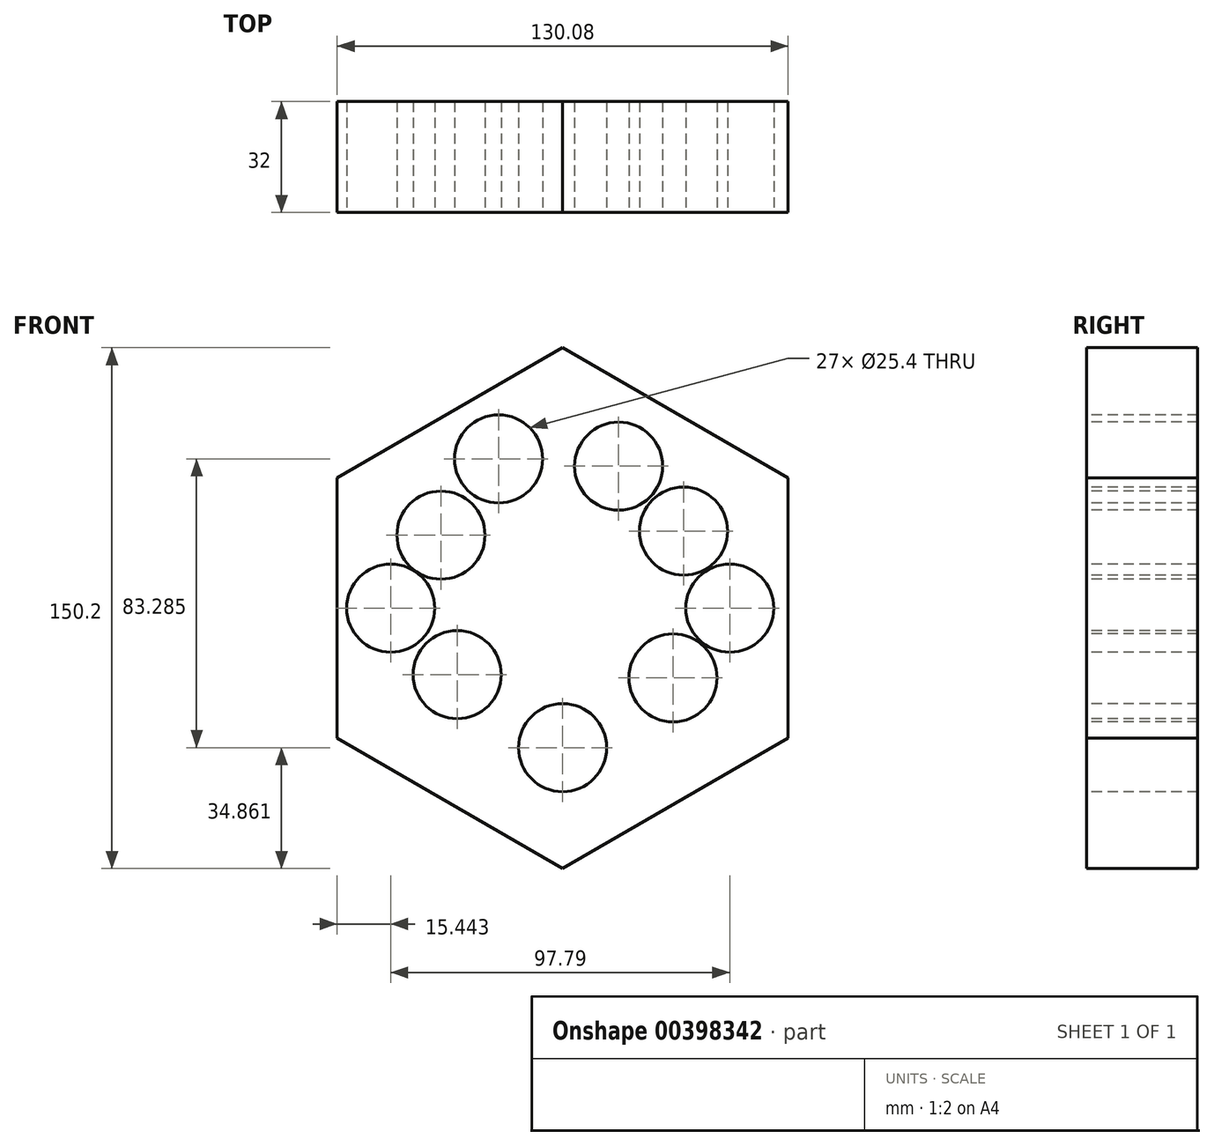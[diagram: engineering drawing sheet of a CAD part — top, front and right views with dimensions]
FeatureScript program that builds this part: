
annotation { "Feature Type Name" : "Feature", "Feature Type Description" : "" }
export const myFeature = defineFeature(function(context is Context, id is Id, definition is map)
    precondition{}
    {
        {
            var Q0;
            Q0=qCreatedBy(makeId("Front.planeOp"),FACE);
            var sketch = newSketch(context, id + "F0", { "sketchPlane" : qUnion([Q0])});
            skCircle(sketch, "E0.cCircle", {"center": v(0, 0) * mm, "radius": 65.04 * mm, "construction": true});
            skLineSegment(sketch, "E0.0", {"start": v(65.04, 37.55) * mm, "end": v(65.04, -37.55) * mm});
            skLineSegment(sketch, "E0.1", {"start": v(65.04, -37.55) * mm, "end": v(0, -75.1) * mm});
            skLineSegment(sketch, "E0.2", {"start": v(0, -75.1) * mm, "end": v(-65.04, -37.55) * mm});
            skLineSegment(sketch, "E0.3", {"start": v(-65.04, -37.55) * mm, "end": v(-65.04, 37.55) * mm});
            skLineSegment(sketch, "E0.4", {"start": v(-65.04, 37.55) * mm, "end": v(0, 75.1) * mm});
            skLineSegment(sketch, "E0.5", {"start": v(0, 75.1) * mm, "end": v(65.04, 37.55) * mm});
            skPoint(sketch, "E0.0.midPoint", {"position": v(65.04, 0) * mm});
            skSolve(sketch);
        }
        {
            var Q0;
            Q0=qCreatedBy(makeId("Front.planeOp"),FACE);
            var sketch = newSketch(context, id + "F1", { "sketchPlane" : qUnion([Q0])});
            skEllipse(sketch, "E1", {"center": v(-35.1, 21.06) * mm, "majorRadius": 29.5 * mm, "minorRadius": 7.58 * mm, "majorAxis": v(0.92, -0.38)});
            skSolve(sketch);
        }
        {
            var Q0;
            Q0=makeQuery(id+"F0.imprint","IMPRINT",FACE,{"disambiguationData":[TD([[makeQuery(id+"F0.imprint","IMPRINT",EDGE,{"derivedFrom":sQuery(id+"F0.wireOp",EDGE,"E0.0")}),-1.0]])]});
            var sketch = newSketch(context, id + "F2", { "sketchPlane" : qUnion([Q0])});
            skEllipse(sketch, "E2", {"center": v(34.86, 22.23) * mm, "majorRadius": 25.9 * mm, "minorRadius": 9.15 * mm, "majorAxis": v(-0.77, -0.64)});
            skSolve(sketch);
        }
        {
            var Q0;
            Q0=makeQuery(id+"F0.imprint","IMPRINT",FACE,{"disambiguationData":[TD([[makeQuery(id+"F0.imprint","IMPRINT",EDGE,{"derivedFrom":sQuery(id+"F0.wireOp",EDGE,"E0.0")}),-1.0]])]});
            var sketch = newSketch(context, id + "F3", { "sketchPlane" : qUnion([Q0])});
            skEllipse(sketch, "E3", {"center": v(-30.41, -19.18) * mm, "majorRadius": 31.91 * mm, "minorRadius": 8.43 * mm, "majorAxis": v(-0.9, -0.45)});
            skSolve(sketch);
        }
        {
            var Q0;
            Q0=makeQuery(id+"F0.imprint","IMPRINT",FACE,{"disambiguationData":[TD([[makeQuery(id+"F0.imprint","IMPRINT",EDGE,{"derivedFrom":sQuery(id+"F0.wireOp",EDGE,"E0.0")}),-1.0]])]});
            var sketch = newSketch(context, id + "F4", { "sketchPlane" : qUnion([Q0])});
            skEllipse(sketch, "E4", {"center": v(31.82, -20.12) * mm, "majorRadius": 33.8 * mm, "minorRadius": 8.23 * mm, "majorAxis": v(0.9, -0.44)});
            skSolve(sketch);
        }
        {
            var Q0;
            Q0=makeQuery(id+"F0.imprint","IMPRINT",FACE,{"disambiguationData":[TD([[makeQuery(id+"F0.imprint","IMPRINT",EDGE,{"derivedFrom":sQuery(id+"F0.wireOp",EDGE,"E0.0")}),-1.0]])]});
            var sketch = newSketch(context, id + "F5", { "sketchPlane" : qUnion([Q0])});
            skCircle(sketch, "E5", {"center": v(-18.48, 43.05) * mm, "radius": 13.64 * mm});
            skSolve(sketch);
        }
        {
            var Q0;
            Q0=makeQuery(id+"F0.imprint","IMPRINT",FACE,{"disambiguationData":[TD([[makeQuery(id+"F0.imprint","IMPRINT",EDGE,{"derivedFrom":sQuery(id+"F0.wireOp",EDGE,"E0.0")}),-1.0]])]});
            var sketch = newSketch(context, id + "F6", { "sketchPlane" : qUnion([Q0])});
            skCircle(sketch, "E6", {"center": v(-49.6, 0) * mm, "radius": 11.14 * mm});
            skSolve(sketch);
        }
        {
            var Q0;
            Q0=makeQuery(id+"F0.imprint","IMPRINT",FACE,{"disambiguationData":[TD([[makeQuery(id+"F0.imprint","IMPRINT",EDGE,{"derivedFrom":sQuery(id+"F0.wireOp",EDGE,"E0.0")}),-1.0]])]});
            var sketch = newSketch(context, id + "F7", { "sketchPlane" : qUnion([Q0])});
            skCircle(sketch, "E7", {"center": v(16.14, 40.94) * mm, "radius": 12.82 * mm});
            skCircle(sketch, "E8", {"center": v(48.2, 0) * mm, "radius": 13.44 * mm});
            skCircle(sketch, "E9", {"center": v(0, -40.24) * mm, "radius": 16.75 * mm});
            skSolve(sketch);
        }
        {
            var Q0;
            Q0=makeQuery(id+"F0.imprint","IMPRINT",FACE,{"disambiguationData":[TD([[makeQuery(id+"F0.imprint","IMPRINT",EDGE,{"derivedFrom":sQuery(id+"F0.wireOp",EDGE,"E0.0")}),-1.0]])]});
            extrude(context, id + "F8", {"entities" : qUnion([Q0]), "oppositeDirection" : true, "depth" : 32 * mm});
        }
        {
            var Q0;
            Q0=sQuery(id+"F5.wireOp",VERTEX,"E5.center");
            var Q1;
            Q1=sQuery(id+"F7.wireOp",VERTEX,"E7.center");
            var Q2;
            Q2=sQuery(id+"F2.wireOp",VERTEX,"E2.center");
            var Q3;
            Q3=sQuery(id+"F7.wireOp",VERTEX,"E8.center");
            var Q4;
            Q4=sQuery(id+"F7.wireOp",VERTEX,"E9.center");
            var Q5;
            Q5=sQuery(id+"F3.wireOp",VERTEX,"E3.center");
            var Q6;
            Q6=sQuery(id+"F6.wireOp",VERTEX,"E6.center");
            var Q7;
            Q7=sQuery(id+"F1.wireOp",VERTEX,"E1.center");
            var Q8;
            Q8=sQuery(id+"F4.wireOp",VERTEX,"E4.center");
            var Q9;
            Q9=makeQuery(id+"F8.opExtrude","SWEPT_BODY",BODY,{"disambiguationData":[OSD([sQuery(id+"F0.wireOp",EDGE,"E0.0"),sQuery(id+"F0.wireOp",EDGE,"E0.1"),sQuery(id+"F0.wireOp",EDGE,"E0.2"),sQuery(id+"F0.wireOp",EDGE,"E0.3"),sQuery(id+"F0.wireOp",EDGE,"E0.4"),sQuery(id+"F0.wireOp",EDGE,"E0.5")])]});
            hole(context, id + "F9", {"style" : HoleStyle.SIMPLE, "endStyle" : HoleEndStyle.THROUGH, "holeDiameter" : 25.4 * mm, "isTappedThrough" : true, "tappedDepth" : 12.7 * mm, "tapClearance" : 3, "locations" : qUnion([Q0, Q1, Q2, Q3, Q4, Q5, Q6, Q7, Q8]), "scope" : qUnion([Q9])});
        }
    });
